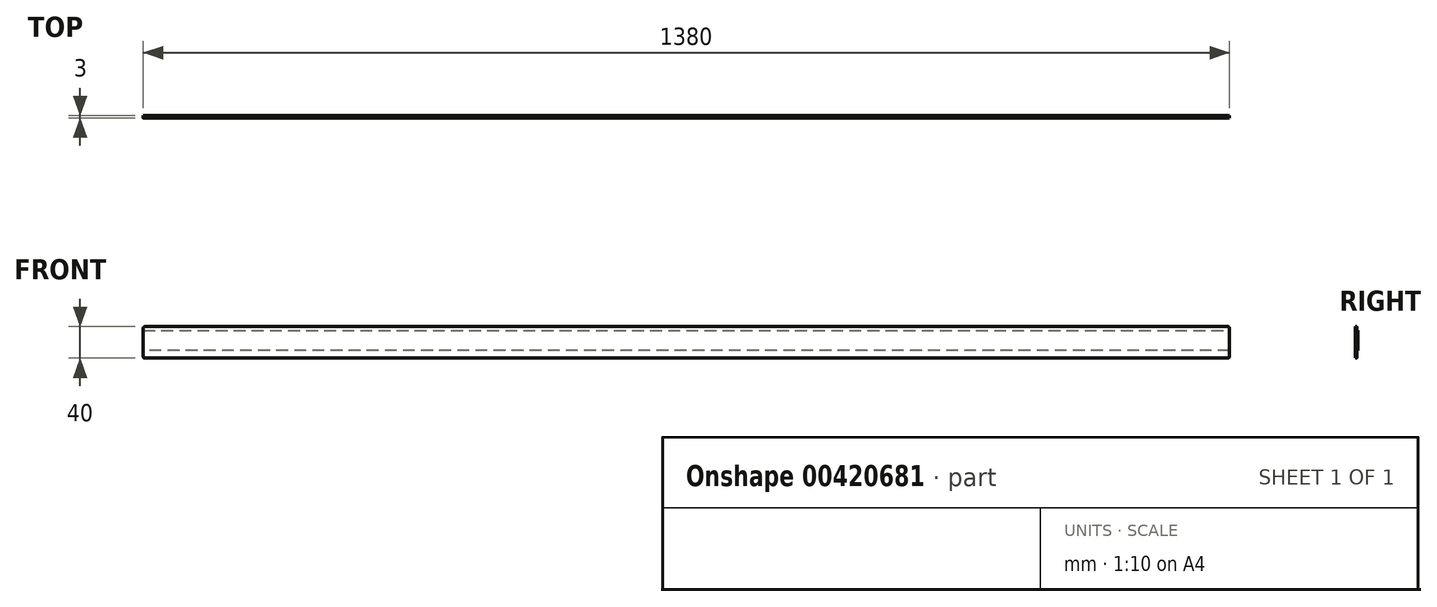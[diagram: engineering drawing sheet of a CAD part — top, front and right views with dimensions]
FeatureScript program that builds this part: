
annotation { "Feature Type Name" : "Feature", "Feature Type Description" : "" }
export const myFeature = defineFeature(function(context is Context, id is Id, definition is map)
    precondition{}
    {
        {
            var Q0;
            Q0=qCreatedBy(makeId("Front.planeOp"),FACE);
            var sketch = newSketch(context, id + "F0", { "sketchPlane" : qUnion([Q0])});
            skLineSegment(sketch, "E0.bottom", {"start": v(690, -20) * mm, "end": v(-690, -20) * mm});
            skLineSegment(sketch, "E0.top", {"start": v(690, 20) * mm, "end": v(-690, 20) * mm});
            skLineSegment(sketch, "E0.left", {"start": v(690, -20) * mm, "end": v(690, 20) * mm});
            skLineSegment(sketch, "E0.right", {"start": v(-690, -20) * mm, "end": v(-690, 20) * mm});
            skPoint(sketch, "E0.middle", {"position": v(0, 0) * mm});
            skSolve(sketch);
        }
        {
            var Q0;
            Q0=qSketchRegion(id+"F0",true);
            extrude(context, id + "F1", {"entities" : qUnion([Q0]), "depth" : 3 * mm});
        }
        {
            var Q0;
            Q0=makeQuery(id+"F1.opExtrude","CAP_FACE",FACE,{"disambiguationData":[OSD([sQuery(id+"F0.wireOp",EDGE,"E0.bottom"),sQuery(id+"F0.wireOp",EDGE,"E0.top"),sQuery(id+"F0.wireOp",EDGE,"E0.left"),sQuery(id+"F0.wireOp",EDGE,"E0.right")])],"isStart":true});
            var sketch = newSketch(context, id + "F2", { "sketchPlane" : qUnion([Q0])});
            skLineSegment(sketch, "E1", {"start": v(-690, 20) * mm, "end": v(690, 20) * mm});
            skLineSegment(sketch, "E2", {"start": v(690, 20) * mm, "end": v(690, 15) * mm});
            skLineSegment(sketch, "E3", {"start": v(690, 15) * mm, "end": v(-690, 15) * mm});
            skLineSegment(sketch, "E4", {"start": v(-690, 15) * mm, "end": v(-690, 20) * mm});
            skLineSegment(sketch, "E5", {"start": v(-690, -20) * mm, "end": v(-690, -10) * mm});
            skLineSegment(sketch, "E6", {"start": v(-690, -10) * mm, "end": v(690, -10) * mm});
            skLineSegment(sketch, "E7", {"start": v(690, -10) * mm, "end": v(690, -20) * mm});
            skLineSegment(sketch, "E8", {"start": v(690, -20) * mm, "end": v(-690, -20) * mm});
            skSolve(sketch);
        }
        {
            var Q0;
            Q0=qSketchRegion(id+"F2",true);
            extrude(context, id + "F3", {"entities" : qUnion([Q0]), "operationType" : NewBodyOperationType.REMOVE, "oppositeDirection" : true, "depth" : 1.5 * mm});
        }
        {
            var Q0;
            Q0=makeQuery(id+"F1.opExtrude","SWEPT_EDGE",EDGE,{"disambiguationData":[OSD([sQuery(id+"F0.wireOp",EDGE,"E0.top"),sQuery(id+"F0.wireOp",EDGE,"E0.left")])]});
            var Q1;
            Q1=makeQuery(id+"F1.opExtrude","SWEPT_EDGE",EDGE,{"disambiguationData":[OSD([sQuery(id+"F0.wireOp",EDGE,"E0.bottom"),sQuery(id+"F0.wireOp",EDGE,"E0.left")])]});
            var Q2;
            Q2=makeQuery(id+"F1.opExtrude","SWEPT_EDGE",EDGE,{"disambiguationData":[OSD([sQuery(id+"F0.wireOp",EDGE,"E0.top"),sQuery(id+"F0.wireOp",EDGE,"E0.right")])]});
            var Q3;
            Q3=makeQuery(id+"F1.opExtrude","SWEPT_EDGE",EDGE,{"disambiguationData":[OSD([sQuery(id+"F0.wireOp",EDGE,"E0.bottom"),sQuery(id+"F0.wireOp",EDGE,"E0.right")])]});
            fillet(context, id + "F4", {"entities" : qUnion([Q0, Q1, Q2, Q3]), "radius" : 2 * mm, "tangentPropagation" : true, "allowEdgeOverflow" : false});
        }
    });
